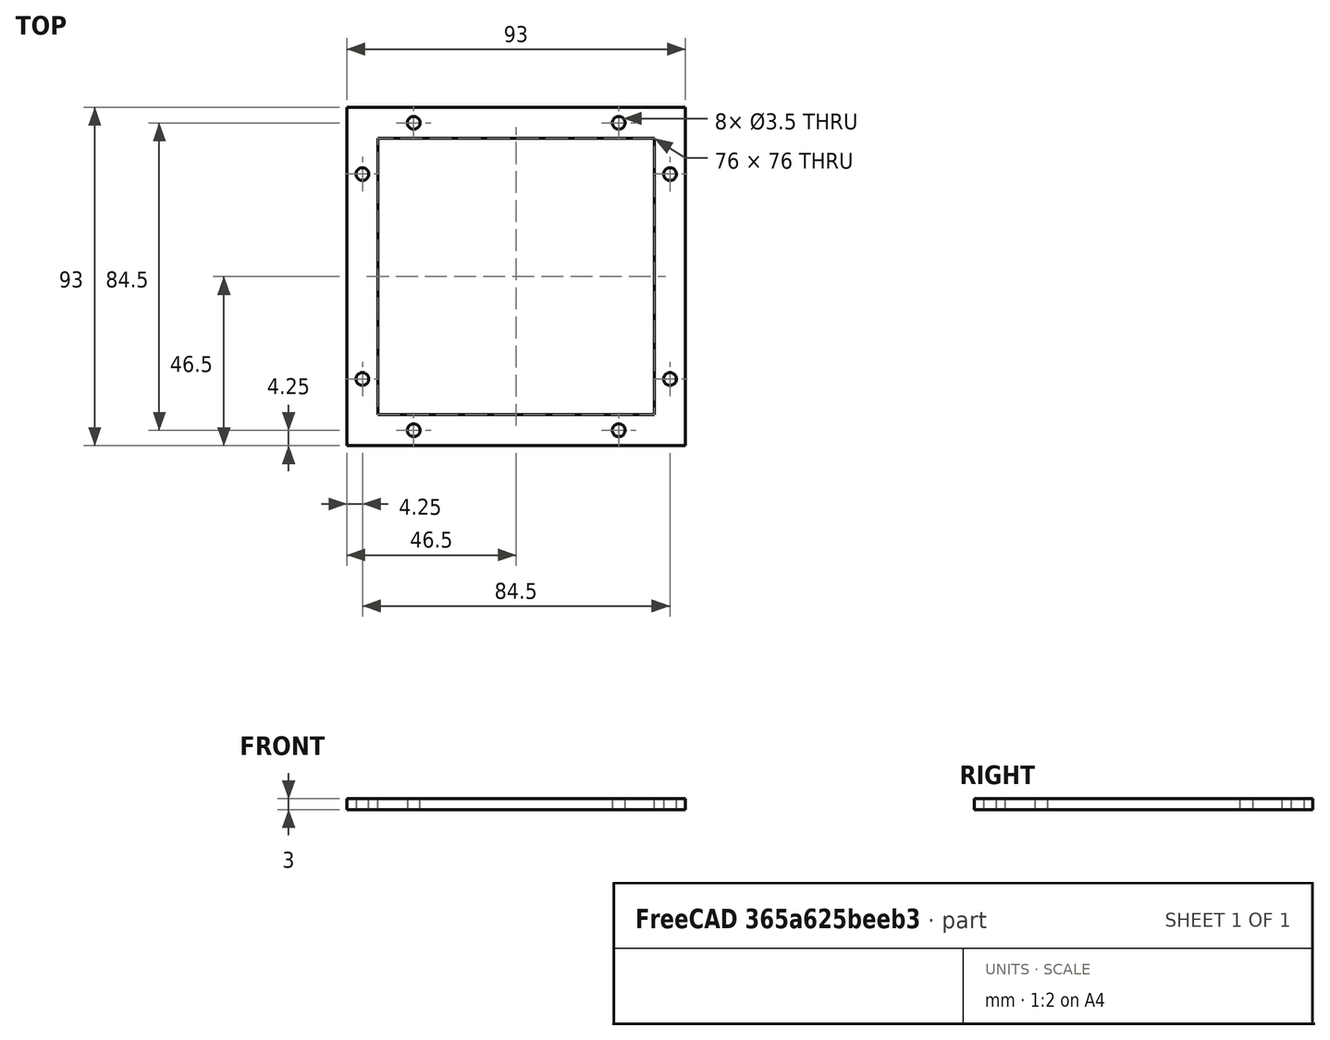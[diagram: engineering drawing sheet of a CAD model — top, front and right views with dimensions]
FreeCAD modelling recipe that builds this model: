
FCSTD DOCUMENT  (FreeCAD 0.14R3141 (Git))
Label: notebook
License: CC-BY 3.0
LicenseURL: http://creativecommons.org/licenses/by/3.0/
objects: Sketcher::SketchObject×3, Drawing::FeatureViewPart×3, PartDesign::Pad×1, Drawing::FeaturePage×1
note: 5 computed .brp shape members not serialized (recipe doc carries the construction recipe); baked Part::Feature solids carry a one-line shape summary decoded from their .brp

FEATURE [Sketcher::SketchObject] Sketch
  sketch-geometry (49):
    g0: LineSegment StartX=-38 StartY=38 StartZ=0 EndX=38 EndY=38 EndZ=0
    g1: LineSegment StartX=38 StartY=38 StartZ=0 EndX=38 EndY=-38 EndZ=0
    g2: LineSegment StartX=38 StartY=-38 StartZ=0 EndX=-38 EndY=-38 EndZ=0
    g3: LineSegment StartX=-38 StartY=-38 StartZ=0 EndX=-38 EndY=38 EndZ=0
    g4: LineSegment [constr] StartX=-38 StartY=0 StartZ=0 EndX=0 EndY=0 EndZ=0
    g5: LineSegment [constr] StartX=0 StartY=0 StartZ=0 EndX=0 EndY=38 EndZ=0
    g6: LineSegment [constr] StartX=0 StartY=0 StartZ=0 EndX=38 EndY=0 EndZ=0
    g7: LineSegment StartX=-46.5 StartY=46.5 StartZ=0 EndX=46.5 EndY=46.5 EndZ=0
    g8: LineSegment StartX=46.5 StartY=46.5 StartZ=0 EndX=46.5 EndY=-46.5 EndZ=0
    g9: LineSegment StartX=46.5 StartY=-46.5 StartZ=0 EndX=-46.5 EndY=-46.5 EndZ=0
    g10: LineSegment StartX=-46.5 StartY=-46.5 StartZ=0 EndX=-46.5 EndY=46.5 EndZ=0
    g11: LineSegment [constr] StartX=-38 StartY=46.5 StartZ=0 EndX=-38 EndY=38 EndZ=0
    g12: LineSegment [constr] StartX=-38 StartY=38 StartZ=0 EndX=-46.5 EndY=38 EndZ=0
    g13: LineSegment [constr] StartX=38 StartY=-38 StartZ=0 EndX=46.5 EndY=-38 EndZ=0
    g14: LineSegment [constr] StartX=-42.25 StartY=46.5 StartZ=0 EndX=-42.25 EndY=42.25 EndZ=0
    g15: LineSegment [constr] StartX=-42.25 StartY=42.25 StartZ=0 EndX=-38 EndY=42.25 EndZ=0
    g16: LineSegment [constr] StartX=-42.25 StartY=42.25 StartZ=0 EndX=-46.5 EndY=42.25 EndZ=0
    g17: LineSegment [constr] StartX=-42.25 StartY=42.25 StartZ=0 EndX=-28.1667 EndY=42.25 EndZ=0
    g18: LineSegment [constr] StartX=-28.1667 StartY=42.25 StartZ=0 EndX=-14.0833 EndY=42.25 EndZ=0
    g19: LineSegment [constr] StartX=-14.0833 StartY=42.25 StartZ=0 EndX=0 EndY=42.25 EndZ=0
    g20: LineSegment [constr] StartX=0 StartY=42.25 StartZ=0 EndX=14.0833 EndY=42.25 EndZ=0
    g21: LineSegment [constr] StartX=14.0833 StartY=42.25 StartZ=0 EndX=28.1667 EndY=42.25 EndZ=0
    g22: LineSegment [constr] StartX=28.1667 StartY=42.25 StartZ=0 EndX=42.25 EndY=42.25 EndZ=0
    g23: LineSegment [constr] StartX=42.25 StartY=42.25 StartZ=0 EndX=42.25 EndY=28.1667 EndZ=0
    g24: LineSegment [constr] StartX=42.25 StartY=28.1667 StartZ=0 EndX=42.25 EndY=14.0833 EndZ=0
    g25: LineSegment [constr] StartX=42.25 StartY=14.0833 StartZ=0 EndX=42.25 EndY=0 EndZ=0
    g26: LineSegment [constr] StartX=42.25 StartY=0 StartZ=0 EndX=42.25 EndY=-14.0833 EndZ=0
    g27: LineSegment [constr] StartX=42.25 StartY=-14.0833 StartZ=0 EndX=42.25 EndY=-28.1667 EndZ=0
    g28: LineSegment [constr] StartX=42.25 StartY=-28.1667 StartZ=0 EndX=42.25 EndY=-42.25 EndZ=0
    g29: LineSegment [constr] StartX=42.25 StartY=-42.25 StartZ=0 EndX=28.1667 EndY=-42.25 EndZ=0
    g30: LineSegment [constr] StartX=28.1667 StartY=-42.25 StartZ=0 EndX=14.0833 EndY=-42.25 EndZ=0
    g31: LineSegment [constr] StartX=14.0833 StartY=-42.25 StartZ=0 EndX=0 EndY=-42.25 EndZ=0
    g32: LineSegment [constr] StartX=0 StartY=-42.25 StartZ=0 EndX=-14.0833 EndY=-42.25 EndZ=0
    g33: LineSegment [constr] StartX=-14.0833 StartY=-42.25 StartZ=0 EndX=-28.1667 EndY=-42.25 EndZ=0
    g34: LineSegment [constr] StartX=-28.1667 StartY=-42.25 StartZ=0 EndX=-42.25 EndY=-42.25 EndZ=0
    g35: LineSegment [constr] StartX=-42.25 StartY=-42.25 StartZ=0 EndX=-42.25 EndY=-28.1667 EndZ=0
    g36: LineSegment [constr] StartX=-42.25 StartY=-28.1667 StartZ=0 EndX=-42.25 EndY=-14.0833 EndZ=0
    g37: LineSegment [constr] StartX=-42.25 StartY=-14.0833 StartZ=0 EndX=-42.25 EndY=0 EndZ=0
    g38: LineSegment [constr] StartX=-42.25 StartY=0 StartZ=0 EndX=-42.25 EndY=14.0833 EndZ=0
    g39: LineSegment [constr] StartX=-42.25 StartY=14.0833 StartZ=0 EndX=-42.25 EndY=28.1667 EndZ=0
    g40: LineSegment [constr] StartX=-42.25 StartY=28.1667 StartZ=0 EndX=-42.25 EndY=42.25 EndZ=0
    g41: Circle CenterX=-28.1667 CenterY=42.25 CenterZ=0 NormalX=0 NormalY=0 NormalZ=1 Radius=1.75
    g42: Circle CenterX=28.1667 CenterY=42.25 CenterZ=0 NormalX=0 NormalY=0 NormalZ=1 Radius=1.75
    g43: Circle CenterX=42.25 CenterY=28.1667 CenterZ=0 NormalX=0 NormalY=0 NormalZ=1 Radius=1.75
    g44: Circle CenterX=42.25 CenterY=-28.1667 CenterZ=0 NormalX=0 NormalY=0 NormalZ=1 Radius=1.75
    g45: Circle CenterX=28.1667 CenterY=-42.25 CenterZ=0 NormalX=0 NormalY=0 NormalZ=1 Radius=1.75
    g46: Circle CenterX=-28.1667 CenterY=-42.25 CenterZ=0 NormalX=0 NormalY=0 NormalZ=1 Radius=1.75
    g47: Circle CenterX=-42.25 CenterY=-28.1667 CenterZ=0 NormalX=0 NormalY=0 NormalZ=1 Radius=1.75
    g48: Circle CenterX=-42.25 CenterY=28.1667 CenterZ=0 NormalX=0 NormalY=0 NormalZ=1 Radius=1.75
  constraints (139):
    c: Coincident(g0,g1)
    c: Coincident(g1,g2)
    c: Coincident(g2,g3)
    c: Coincident(g3,g0)
    c: Horizontal(g0)
    c: Horizontal(g2)
    c: Vertical(g1)
    c: Vertical(g3)
    c: PointOnObject(g4,g3)
    c: Coincident(g4,g-1)
    c: Horizontal(g4)
    c: Coincident(g4,g5)
    c: PointOnObject(g5,g0)
    c: Vertical(g5)
    c: Coincident(g6,g-1)
    c: PointOnObject(g6,g1)
    c: Horizontal(g6)
    c: Equal(g5,g4)
    c: Equal(g6,g5)
    c: Equal(g2,g3)
    c: DistanceY(g3) = 76
    c: Coincident(g7,g8)
    c: Coincident(g8,g9)
    c: Coincident(g9,g10)
    c: Coincident(g10,g7)
    c: Horizontal(g7)
    c: Horizontal(g9)
    c: Vertical(g8)
    c: Vertical(g10)
    c: Equal(g9,g10)
    c: PointOnObject(g11,g7)
    c: Coincident(g11,g0)
    c: Vertical(g11)
    c: Coincident(g11,g12)
    c: PointOnObject(g12,g10)
    c: Horizontal(g12)
    c: Equal(g11,g12)
    c: Coincident(g13,g1)
    c: PointOnObject(g13,g8)
    c: Horizontal(g13)
    c: Equal(g13,g11)
    c: DistanceY(g11) = -8.5
    c: PointOnObject(g14,g7)
    c: Vertical(g14)
    c: Coincident(g15,g14)
    c: PointOnObject(g15,g11)
    c: Horizontal(g15)
    c: Coincident(g16,g14)
    c: PointOnObject(g16,g10)
    c: Horizontal(g16)
    c: Equal(g16,g14)
    c: Equal(g14,g15)
    c: Coincident(g14,g17)
    c: Horizontal(g17)
    c: Coincident(g17,g18)
    c: Horizontal(g18)
    c: Coincident(g18,g19)
    c: Horizontal(g19)
    c: Coincident(g19,g20)
    c: Horizontal(g20)
    c: Coincident(g20,g21)
    c: Horizontal(g21)
    c: Coincident(g21,g22)
    c: Horizontal(g22)
    c: Coincident(g22,g23)
    c: Vertical(g23)
    c: Coincident(g23,g24)
    c: Vertical(g24)
    c: Coincident(g24,g25)
    c: Vertical(g25)
    c: Coincident(g25,g26)
    c: Vertical(g26)
    c: Coincident(g26,g27)
    c: Vertical(g27)
    c: Coincident(g27,g28)
    c: Vertical(g28)
    c: Coincident(g28,g29)
    c: Horizontal(g29)
    c: Coincident(g29,g30)
    c: Horizontal(g30)
    c: Coincident(g30,g31)
    c: PointOnObject(g31,g-2)
    c: Horizontal(g31)
    c: Coincident(g31,g32)
    c: Horizontal(g32)
    c: Coincident(g32,g33)
    c: Horizontal(g33)
    c: Coincident(g33,g34)
    c: Horizontal(g34)
    c: Coincident(g34,g35)
    c: Vertical(g35)
    c: Coincident(g35,g36)
    c: Vertical(g36)
    c: Coincident(g36,g37)
    c: PointOnObject(g37,g-1)
    c: Vertical(g37)
    c: Coincident(g37,g38)
    c: Vertical(g38)
    c: Coincident(g38,g39)
    c: Vertical(g39)
    c: Coincident(g39,g40)
    c: Coincident(g40,g14)
    c: Vertical(g40)
    c: PointOnObject(g19,g-2)
    c: PointOnObject(g25,g-1)
    c: Equal(g17,g18)
    c: Equal(g18,g19)
    c: Equal(g20,g21)
    c: Equal(g21,g22)
    c: Equal(g20,g19)
    c: Equal(g23,g24)
    c: Equal(g24,g25)
    c: Equal(g25,g26)
    c: Equal(g26,g27)
    c: Equal(g27,g28)
    c: Equal(g29,g30)
    c: Equal(g30,g31)
    c: Equal(g32,g33)
    c: Equal(g35,g36)
    c: Equal(g36,g37)
    c: Equal(g40,g39)
    c: Equal(g39,g38)
    c: Equal(g34,g33)
    c: Coincident(g41,g17)
    c: Coincident(g42,g21)
    c: Coincident(g43,g23)
    c: Coincident(g44,g27)
    c: Coincident(g45,g29)
    c: Coincident(g46,g33)
    c: Coincident(g47,g35)
    c: Coincident(g48,g39)
    c: Radius(g41) = 1.75
    c: Equal(g42,g43)
    c: Equal(g44,g45)
    c: Equal(g46,g47)
    c: Equal(g41,g42)
    c: Equal(g43,g44)
    c: Equal(g45,g46)
    c: Equal(g47,g48)
FEATURE [PartDesign::Pad] Pad  label="Base data"
  Length = 3
  Length2 = 100
  Sketch = -> Sketch
  Type = 0
FEATURE [Sketcher::SketchObject] Sketch001  label="Everything"
  ExternalGeometry = -> [Pad]
  Placement = pos=(0,0,3) rot=(0,0,1;0rad)
  Support = -> Pad [Face18]
  sketch-geometry (62):
    g0: LineSegment StartX=-49.5 StartY=49.5 StartZ=0 EndX=49.5 EndY=49.5 EndZ=0
    g1: LineSegment [constr] StartX=49.5 StartY=49.5 StartZ=0 EndX=49.5 EndY=-49.5 EndZ=0
    g2: LineSegment StartX=49.5 StartY=-49.5 StartZ=0 EndX=-49.5 EndY=-49.5 EndZ=0
    g3: LineSegment [constr] StartX=-49.5 StartY=-49.5 StartZ=0 EndX=-49.5 EndY=49.5 EndZ=0
    g4: LineSegment [constr] StartX=-46.5 StartY=49.5 StartZ=0 EndX=-46.5 EndY=46.5 EndZ=0
    g5: LineSegment [constr] StartX=-46.5 StartY=46.5 StartZ=0 EndX=-49.5 EndY=46.5 EndZ=0
    g6: LineSegment [constr] StartX=46.5 StartY=-46.5 StartZ=0 EndX=49.5 EndY=-46.5 EndZ=0
    g7: LineSegment StartX=49.5 StartY=49.5 StartZ=0 EndX=69.5 EndY=49.5 EndZ=0
    g8: LineSegment [constr] StartX=69.5 StartY=49.5 StartZ=0 EndX=69.5 EndY=-49.5 EndZ=0
    g9: LineSegment StartX=69.5 StartY=-49.5 StartZ=0 EndX=49.5 EndY=-49.5 EndZ=0
    g10: LineSegment StartX=69.5 StartY=49.5 StartZ=0 EndX=165.5 EndY=49.5 EndZ=0
    g11: LineSegment StartX=168.5 StartY=46.5 StartZ=0 EndX=168.5 EndY=-46.5 EndZ=0
    g12: LineSegment StartX=165.5 StartY=-49.5 StartZ=0 EndX=69.5 EndY=-49.5 EndZ=0
    g13: ArcOfCircle CenterX=165.5 CenterY=46.5 CenterZ=0 NormalX=0 NormalY=0 NormalZ=1 Radius=3 StartAngle=0 EndAngle=1.5708
    g14: ArcOfCircle CenterX=165.5 CenterY=-46.5 CenterZ=0 NormalX=0 NormalY=0 NormalZ=1 Radius=3 StartAngle=4.71239 EndAngle=6.28319
    g15: LineSegment StartX=72.5 StartY=-46.5 StartZ=0 EndX=165.5 EndY=-46.5 EndZ=0
    g16: LineSegment StartX=165.5 StartY=-46.5 StartZ=0 EndX=165.5 EndY=46.5 EndZ=0
    g17: LineSegment StartX=165.5 StartY=46.5 StartZ=0 EndX=150.5 EndY=46.5 EndZ=0
    g18: LineSegment StartX=72.5 StartY=-31.5 StartZ=0 EndX=72.5 EndY=-46.5 EndZ=0
    g19: LineSegment [constr] StartX=72.5 StartY=-46.5 StartZ=0 EndX=69.5 EndY=-46.5 EndZ=0
    g20: LineSegment [constr] StartX=161.25 StartY=42.25 StartZ=0 EndX=161.25 EndY=14.0833 EndZ=0
    g21: LineSegment [constr] StartX=161.25 StartY=14.0833 StartZ=0 EndX=161.25 EndY=-14.0833 EndZ=0
    g22: LineSegment [constr] StartX=161.25 StartY=-14.0833 StartZ=0 EndX=161.25 EndY=-42.25 EndZ=0
    g23: LineSegment [constr] StartX=161.25 StartY=-42.25 StartZ=0 EndX=133.083 EndY=-42.25 EndZ=0
    g24: LineSegment [constr] StartX=133.083 StartY=-42.25 StartZ=0 EndX=104.917 EndY=-42.25 EndZ=0
    g25: LineSegment [constr] StartX=104.917 StartY=-42.25 StartZ=0 EndX=76.75 EndY=-42.25 EndZ=0
    g26: LineSegment [constr] StartX=-28.1667 StartY=42.25 StartZ=0 EndX=0 EndY=42.25 EndZ=0
    g27: LineSegment [constr] StartX=161.25 StartY=-46.5 StartZ=0 EndX=161.25 EndY=-42.25 EndZ=0
    g28: LineSegment [constr] StartX=161.25 StartY=-42.25 StartZ=0 EndX=165.5 EndY=-42.25 EndZ=0
    g29: Circle CenterX=161.25 CenterY=42.25 CenterZ=0 NormalX=0 NormalY=0 NormalZ=1 Radius=1.75
    g30: Circle CenterX=161.25 CenterY=14.0833 CenterZ=0 NormalX=0 NormalY=0 NormalZ=1 Radius=1.75
    g31: Circle CenterX=161.25 CenterY=-14.0833 CenterZ=0 NormalX=0 NormalY=0 NormalZ=1 Radius=1.75
    g32: Circle CenterX=161.25 CenterY=-42.25 CenterZ=0 NormalX=0 NormalY=0 NormalZ=1 Radius=1.75
    g33: Circle CenterX=133.083 CenterY=-42.25 CenterZ=0 NormalX=0 NormalY=0 NormalZ=1 Radius=1.75
    g34: Circle CenterX=104.917 CenterY=-42.25 CenterZ=0 NormalX=0 NormalY=0 NormalZ=1 Radius=1.75
    g35: Circle CenterX=76.75 CenterY=-42.25 CenterZ=0 NormalX=0 NormalY=0 NormalZ=1 Radius=1.75
    g36: LineSegment StartX=66 StartY=34.5 StartZ=0 EndX=53 EndY=34.5 EndZ=0
    g37: LineSegment [constr] StartX=53 StartY=34.5 StartZ=0 EndX=53 EndY=24.5 EndZ=0
    g38: LineSegment StartX=53 StartY=24.5 StartZ=0 EndX=66 EndY=24.5 EndZ=0
    g39: LineSegment [constr] StartX=66 StartY=34.5 StartZ=0 EndX=69.5 EndY=34.5 EndZ=0
    g40: LineSegment [constr] StartX=53 StartY=34.5 StartZ=0 EndX=49.5 EndY=34.5 EndZ=0
    g41: ArcOfCircle CenterX=53 CenterY=36 CenterZ=0 NormalX=0 NormalY=0 NormalZ=1 Radius=1.5 StartAngle=3.66519 EndAngle=4.71239
    g42: ArcOfCircle CenterX=50.4019 CenterY=34.5 CenterZ=0 NormalX=0 NormalY=0 NormalZ=1 Radius=1.5 StartAngle=0.523596 EndAngle=5.75958
    g43: ArcOfCircle CenterX=53 CenterY=33 CenterZ=0 NormalX=0 NormalY=0 NormalZ=1 Radius=1.5 StartAngle=1.5708 EndAngle=2.618
    g44: ArcOfCircle CenterX=68.5981 CenterY=34.5 CenterZ=0 NormalX=0 NormalY=0 NormalZ=1 Radius=1.5 StartAngle=3.66519 EndAngle=8.90118
    g45: ArcOfCircle CenterX=66 CenterY=36 CenterZ=0 NormalX=0 NormalY=0 NormalZ=1 Radius=1.5 StartAngle=4.71239 EndAngle=5.75958
    g46: ArcOfCircle CenterX=66 CenterY=33 CenterZ=0 NormalX=0 NormalY=0 NormalZ=1 Radius=1.5 StartAngle=0.523597 EndAngle=1.5708
    g47: ArcOfCircle CenterX=68.5981 CenterY=24.5 CenterZ=0 NormalX=0 NormalY=0 NormalZ=1 Radius=1.5 StartAngle=3.66519 EndAngle=8.90118
    g48: ArcOfCircle CenterX=66 CenterY=26 CenterZ=0 NormalX=0 NormalY=0 NormalZ=1 Radius=1.5 StartAngle=4.71239 EndAngle=5.75959
    g49: ArcOfCircle CenterX=66 CenterY=23 CenterZ=0 NormalX=0 NormalY=0 NormalZ=1 Radius=1.5 StartAngle=0.523598 EndAngle=1.5708
    g50: ArcOfCircle CenterX=50.4019 CenterY=24.5 CenterZ=0 NormalX=0 NormalY=0 NormalZ=1 Radius=1.5 StartAngle=0.523599 EndAngle=5.75959
    g51: ArcOfCircle CenterX=53 CenterY=26 CenterZ=0 NormalX=0 NormalY=0 NormalZ=1 Radius=1.5 StartAngle=3.66519 EndAngle=4.71239
    g52: ArcOfCircle CenterX=53 CenterY=23 CenterZ=0 NormalX=0 NormalY=0 NormalZ=1 Radius=1.5 StartAngle=1.5708 EndAngle=2.61799
    g53: ArcOfCircle CenterX=-49.5 CenterY=39.5 CenterZ=0 NormalX=0 NormalY=0 NormalZ=1 Radius=10 StartAngle=1.5708 EndAngle=2.5806
    g54: ArcOfCircle CenterX=-49.5 CenterY=-39.5 CenterZ=0 NormalX=0 NormalY=0 NormalZ=1 Radius=10 StartAngle=3.70258 EndAngle=4.71239
    g55: LineSegment StartX=-57.9673 StartY=44.8202 StartZ=0 EndX=-83.1206 EndY=4.78822 EndZ=0
    g56: LineSegment StartX=-83.1206 StartY=-4.78822 StartZ=0 EndX=-57.9673 EndY=-44.8202 EndZ=0
    g57: ArcOfCircle CenterX=-75.5 CenterY=0 CenterZ=0 NormalX=0 NormalY=0 NormalZ=1 Radius=9 StartAngle=2.5806 EndAngle=3.70258
    g58: Circle CenterX=-75.5 CenterY=0 CenterZ=0 NormalX=0 NormalY=0 NormalZ=1 Radius=1.75
    g59: LineSegment [constr] StartX=-70.5 StartY=24.8741 StartZ=0 EndX=-70.5 EndY=-24.8741 EndZ=0
    g60: Circle CenterX=158.5 CenterY=0 CenterZ=0 NormalX=0 NormalY=0 NormalZ=1 Radius=1.75
    g61: ArcOfCircle CenterX=217.703 CenterY=-98.7026 CenterZ=0 NormalX=0 NormalY=0 NormalZ=1 Radius=160 StartAngle=2.00426 EndAngle=2.70813
  constraints (184):
    c: Coincident(g0,g1)
    c: Coincident(g1,g2)
    c: Coincident(g2,g3)
    c: Coincident(g3,g0)
    c: Horizontal(g0)
    c: Horizontal(g2)
    c: Vertical(g1)
    c: Vertical(g3)
    c: PointOnObject(g4,g0)
    c: Coincident(g4,g-6)
    c: Vertical(g4)
    c: Coincident(g4,g5)
    c: Horizontal(g5)
    c: Equal(g5,g4)
    c: PointOnObject(g5,g3)
    c: Equal(g3,g2)
    c: Coincident(g6,g-5)
    c: PointOnObject(g6,g1)
    c: Horizontal(g6)
    c: Equal(g6,g4)
    c: Coincident(g0,g7)
    c: Horizontal(g7)
    c: Coincident(g7,g8)
    c: Vertical(g8)
    c: Coincident(g8,g9)
    c: Coincident(g9,g1)
    c: Horizontal(g9)
    c: DistanceX(g7) = 20
    c: Coincident(g7,g10)
    c: Horizontal(g10)
    c: Vertical(g11)
    c: Coincident(g12,g8)
    c: Horizontal(g12)
    c: Tangent(g10,g13)
    c: Tangent(g11,g13)
    c: Tangent(g11,g14)
    c: Tangent(g12,g14)
    c: Horizontal(g15)
    c: Coincident(g15,g16)
    c: Vertical(g16)
    c: Coincident(g16,g17)
    c: Horizontal(g17)
    c: Vertical(g18)
    c: Coincident(g15,g18)
    c: PointOnObject(g15,g-5)
    c: PointOnObject(g16,g-3)
    c: Equal(g15,g16)
    c: Equal(g18,g17)
    c: Coincident(g13,g16)
    c: Equal(g14,g13)
    c: Coincident(g19,g15)
    c: PointOnObject(g19,g8)
    c: Horizontal(g19)
    c: Equal(g19,g6)
    c: DistanceX(g17) = -15
    c: Coincident(g20,g21)
    c: Coincident(g21,g22)
    c: Coincident(g22,g23)
    c: Coincident(g23,g24)
    c: Coincident(g24,g25)
    c: Vertical(g22)
    c: Vertical(g21)
    c: Vertical(g20)
    c: Horizontal(g23)
    c: Horizontal(g24)
    c: Horizontal(g25)
    c: Coincident(g26,g-7)
    c: PointOnObject(g20,g26)
    c: Equal(g20,g26)
    c: Equal(g20,g21)
    c: Equal(g21,g22)
    c: Equal(g23,g22)
    c: Equal(g23,g24)
    c: Equal(g24,g25)
    c: Coincident(g27,g28)
    c: PointOnObject(g27,g15)
    c: Coincident(g27,g22)
    c: PointOnObject(g28,g16)
    c: Horizontal(g28)
    c: Vertical(g27)
    c: Equal(g27,g28)
    c: DistanceX(g5) = -3
    c: Coincident(g29,g20)
    c: Coincident(g30,g20)
    c: Coincident(g31,g21)
    c: Coincident(g32,g22)
    c: Coincident(g33,g23)
    c: Coincident(g34,g24)
    c: Coincident(g35,g25)
    c: Equal(g29,g30)
    c: Equal(g30,g31)
    c: Equal(g31,g32)
    c: Equal(g33,g32)
    c: Equal(g33,g34)
    c: Equal(g34,g35)
    c: Horizontal(g36)
    c: Coincident(g36,g37)
    c: Vertical(g37)
    c: Coincident(g37,g38)
    c: Horizontal(g38)
    c: Equal(g38,g36)
    c: Coincident(g39,g36)
    c: PointOnObject(g39,g8)
    c: Horizontal(g39)
    c: Coincident(g40,g36)
    c: PointOnObject(g40,g1)
    c: Horizontal(g40)
    c: Equal(g40,g39)
    c: Coincident(g41,g36)
    c: PointOnObject(g42,g40)
    c: Coincident(g42,g41)
    c: Coincident(g43,g36)
    c: Coincident(g43,g42)
    c: Tangent(g43,g42)
    c: Tangent(g41,g42)
    c: Tangent(g41,g36)
    c: Tangent(g43,g36)
    c: DistanceY(g37) = -10
    c: DistanceY(g39,g7) = 15
    c: Equal(g41,g42)
    c: Radius(g42) = 1.5
    c: PointOnObject(g44,g39)
    c: Coincident(g45,g36)
    c: Coincident(g46,g36)
    c: Coincident(g44,g45)
    c: Coincident(g46,g44)
    c: Equal(g45,g44)
    c: Equal(g46,g45)
    c: Tangent(g45,g44)
    c: Tangent(g46,g44)
    c: Tangent(g45,g36)
    c: Equal(g44,g42)
    c: DistanceX(g36) = -13
    c: Coincident(g48,g38)
    c: Coincident(g49,g38)
    c: Coincident(g48,g47)
    c: Coincident(g49,g47)
    c: Equal(g48,g49)
    c: Equal(g48,g47)
    c: Equal(g47,g44)
    c: Tangent(g48,g47)
    c: Tangent(g49,g47)
    c: Tangent(g49,g38)
    c: Tangent(g48,g38)
    c: Coincident(g51,g37)
    c: Coincident(g52,g37)
    c: Coincident(g51,g50)
    c: Coincident(g52,g50)
    c: Equal(g50,g51)
    c: Equal(g51,g52)
    c: Equal(g50,g42)
    c: Tangent(g51,g50)
    c: Tangent(g52,g50)
    c: Tangent(g51,g38)
    c: Tangent(g52,g38)
    c: PointOnObject(g53,g3)
    c: Coincident(g53,g0)
    c: PointOnObject(g54,g3)
    c: Coincident(g54,g2)
    c: Equal(g54,g53)
    c: Tangent(g53,g55)
    c: Coincident(g56,g54)
    c: Tangent(g56,g54)
    c: Tangent(g55,g57)
    c: Tangent(g56,g57)
    c: PointOnObject(g57,g-1)
    c: Coincident(g58,g57)
    c: Radius(g53) = 10
    c: Vertical(g59)
    c: PointOnObject(g59,g55)
    c: PointOnObject(g59,g56)
    c: DistanceX(g57,g59) = 5
    c: Radius(g58) = 1.75
    c: Radius(g57) = 9
    c: PointOnObject(g60,g-1)
    c: Equal(g58,g60)
    c: Coincident(g61,g17)
    c: Coincident(g61,g18)
    c: Radius(g61) = 160
    c: DistanceX(g59,g2) = 21
    c: DistanceX(g60,g14) = 7
    c: Horizontal(g26)
    c: PointOnObject(g26,g-2)
    c: Equal(g-7,g35)
FEATURE [Drawing::FeatureViewPart] View  label="View: Base"
  Direction = (0,0,-1)
  HiddenWidth = 0.15
  LineWidth = 0.35
  Rotation = 270
  ShowHiddenLines = false
  ShowSmoothLines = false
  Source = -> Pad
  Tolerance = 0.05
  ViewResult = <g id="View: Base"    transform="rotate(270,50,251) translate(50,251) scale(1,1)"   > <g   stroke="rgb(0, 0, 0)"    stroke-width="0.35"    stroke-linecap="butt"    stroke-linejoin="miter"    fill="none"    transform="scale(1,-1)"   > <path id= "1" d=" M 46.5 46.5 L -46.5 46.5 " /> <path id= "2" d=" M -46.5 46.5 L -46.5 -46.5 " /> <path id= "3" d=" M -46.5 -46.5 L 46.5 -46.5 " /> <path id= "4" d=" M 46.5 -46.5 L 46.5 46.5 " /> <path id= "5" d=" M 38 38 L -38 38 " /> <path id= "6" d=" M -38 38 L -38 -38 " /> <path id= "7" d=" M -38 -38 L 38 -38 " /> <path id= "8" d=" M 38 -38 L 38 38 " /> <circle cx ="42.25" cy ="28.1667" r ="1.75" /><circle cx ="42.25" cy ="-28.1667" r ="1.75" /><circle cx ="28.1667" cy ="-42.25" r ="1.75" /><circle cx ="-28.1667" cy ="-42.25" r ="1.75" /><circle cx ="-42.25" cy ="-28.1667" r ="1.75" /><circle cx ="-42.25" cy ="28.1667" r ="1.75" /><circle cx ="-28.1667" cy ="42.25" r ="1.75" /><circle cx ="28.1667" cy ="42.25" r ="1.75" /></g> </g> 
  X = 50
  Y = 251
FEATURE [Drawing::FeatureViewPart] View001  label="View: Everything"
  Direction = (0,0,-1)
  HiddenWidth = 0.15
  LineWidth = 0.35
  Rotation = 270
  ShowHiddenLines = false
  ShowSmoothLines = false
  Source = -> Sketch001
  Tolerance = 0.05
  ViewResult = <blob: 2383 chars omitted>
  X = 50
  Y = 251
FEATURE [Sketcher::SketchObject] Sketch002  label="Border"
  ExternalGeometry = -> [Pad]
  Placement = pos=(0,0,3) rot=(0,0,1;0rad)
  Support = -> Pad [Face18]
  sketch-geometry (24):
    g0: ArcOfCircle CenterX=-23.5 CenterY=38 CenterZ=0 NormalX=0 NormalY=0 NormalZ=1 Radius=8.5 StartAngle=0 EndAngle=1.5708
    g1: LineSegment StartX=-15 StartY=38 StartZ=0 EndX=-38 EndY=38 EndZ=0
    g2: LineSegment StartX=-38 StartY=38 StartZ=0 EndX=-38 EndY=15 EndZ=0
    g3: LineSegment StartX=-23.5 StartY=46.5 StartZ=0 EndX=-46.5 EndY=46.5 EndZ=0
    g4: LineSegment StartX=-46.5 StartY=46.5 StartZ=0 EndX=-46.5 EndY=23.5 EndZ=0
    g5: ArcOfCircle CenterX=-38 CenterY=23.5 CenterZ=0 NormalX=0 NormalY=0 NormalZ=1 Radius=8.5 StartAngle=3.1416 EndAngle=4.71239
    g6: LineSegment StartX=15 StartY=38 StartZ=0 EndX=38 EndY=38 EndZ=0
    g7: LineSegment StartX=38 StartY=38 StartZ=0 EndX=38 EndY=15 EndZ=0
    g8: ArcOfCircle CenterX=23.5 CenterY=38 CenterZ=0 NormalX=0 NormalY=0 NormalZ=1 Radius=8.5 StartAngle=1.5708 EndAngle=3.14159
    g9: ArcOfCircle CenterX=38 CenterY=23.5 CenterZ=0 NormalX=0 NormalY=0 NormalZ=1 Radius=8.5 StartAngle=4.71239 EndAngle=6.28318
    g10: LineSegment StartX=23.5 StartY=46.5 StartZ=0 EndX=46.5 EndY=46.5 EndZ=0
    g11: LineSegment StartX=46.5 StartY=46.5 StartZ=0 EndX=46.5 EndY=23.5 EndZ=0
    g12: LineSegment StartX=-38 StartY=-15 StartZ=0 EndX=-38 EndY=-38 EndZ=0
    g13: LineSegment StartX=-38 StartY=-38 StartZ=0 EndX=-15 EndY=-38 EndZ=0
    g14: LineSegment StartX=-46.5 StartY=-23.5 StartZ=0 EndX=-46.5 EndY=-46.5 EndZ=0
    g15: LineSegment StartX=-46.5 StartY=-46.5 StartZ=0 EndX=-23.5 EndY=-46.5 EndZ=0
    g16: ArcOfCircle CenterX=-38 CenterY=-23.5 CenterZ=0 NormalX=0 NormalY=0 NormalZ=1 Radius=8.5 StartAngle=1.5708 EndAngle=3.14159
    g17: ArcOfCircle CenterX=-23.5 CenterY=-38 CenterZ=0 NormalX=0 NormalY=0 NormalZ=1 Radius=8.5 StartAngle=4.71239 EndAngle=6.28319
    g18: LineSegment StartX=38 StartY=-15 StartZ=0 EndX=38 EndY=-38 EndZ=0
    g19: LineSegment StartX=38 StartY=-38 StartZ=0 EndX=15 EndY=-38 EndZ=0
    g20: LineSegment StartX=23.5 StartY=-46.5 StartZ=0 EndX=46.5 EndY=-46.5 EndZ=0
    g21: LineSegment StartX=46.5 StartY=-46.5 StartZ=0 EndX=46.5 EndY=-23.5 EndZ=0
    g22: ArcOfCircle CenterX=38 CenterY=-23.5 CenterZ=0 NormalX=0 NormalY=0 NormalZ=1 Radius=8.5 StartAngle=4.82221e-06 EndAngle=1.5708
    g23: ArcOfCircle CenterX=23.5 CenterY=-38 CenterZ=0 NormalX=0 NormalY=0 NormalZ=1 Radius=8.5 StartAngle=3.14159 EndAngle=4.71238
  constraints (70):
    c: Horizontal(g1)
    c: Coincident(g1,g2)
    c: Vertical(g2)
    c: PointOnObject(g0,g1)
    c: Coincident(g0,g1)
    c: Tangent(g0,g3)
    c: Coincident(g3,g4)
    c: Vertical(g4)
    c: Horizontal(g3)
    c: PointOnObject(g5,g2)
    c: Coincident(g5,g2)
    c: Coincident(g5,g4)
    c: Equal(g1,g2)
    c: Coincident(g1,g-4)
    c: Coincident(g3,g-6)
    c: Tangent(g4,g5)
    c: Horizontal(g6)
    c: Coincident(g6,g7)
    c: Vertical(g7)
    c: PointOnObject(g8,g6)
    c: Coincident(g8,g6)
    c: PointOnObject(g9,g7)
    c: Coincident(g9,g7)
    c: Tangent(g8,g10)
    c: Coincident(g10,g11)
    c: Coincident(g11,g9)
    c: Equal(g7,g6)
    c: Vertical(g11)
    c: Horizontal(g10)
    c: Tangent(g9,g11)
    c: Equal(g6,g1)
    c: Coincident(g6,g-8)
    c: Coincident(g10,g-7)
    c: Vertical(g12)
    c: Coincident(g12,g13)
    c: Horizontal(g13)
    c: Vertical(g14)
    c: Coincident(g14,g15)
    c: Horizontal(g15)
    c: PointOnObject(g16,g12)
    c: Coincident(g16,g12)
    c: Coincident(g16,g14)
    c: PointOnObject(g17,g13)
    c: Coincident(g17,g13)
    c: Coincident(g17,g15)
    c: Tangent(g17,g15)
    c: Tangent(g14,g16)
    c: Equal(g12,g13)
    c: Equal(g12,g2)
    c: Coincident(g12,g-9)
    c: Coincident(g14,g-10)
    c: Vertical(g18)
    c: Coincident(g18,g19)
    c: Horizontal(g19)
    c: Horizontal(g20)
    c: Coincident(g20,g21)
    c: Vertical(g21)
    c: PointOnObject(g22,g18)
    c: Coincident(g22,g18)
    c: Coincident(g22,g21)
    c: PointOnObject(g23,g19)
    c: Coincident(g23,g19)
    c: Coincident(g23,g20)
    c: Tangent(g23,g20)
    c: Tangent(g22,g21)
    c: Coincident(g18,g-9)
    c: Coincident(g20,g-10)
    c: Equal(g18,g19)
    c: Equal(g18,g7)
    c: DistanceX(g0,g6) = 30
FEATURE [Drawing::FeatureViewPart] Ortho  label="View: Border"
  Direction = (0,0,-1)
  HiddenWidth = 0.15
  LineWidth = 0.35
  Rotation = 270
  ShowHiddenLines = false
  ShowSmoothLines = false
  Source = -> Sketch002
  Tolerance = 0.05
  ViewResult = <g id="View: Border"    transform="rotate(270,50,251) translate(50,251) scale(1,1)"   > <g   stroke="rgb(0, 0, 0)"    stroke-width="0.35"    stroke-linecap="butt"    stroke-linejoin="miter"    fill="none"    transform="scale(1,-1)"   > <path d="M15 38 A8.5 8.5 0 0 0 23.5 46.5" /><path id= "2" d=" M 23.5 46.5 L 46.5 46.5 " /> <path id= "3" d=" M 46.5 46.5 L 46.5 23.5 " /> <path d="M46.5 23.5 A8.5 8.5 0 0 0 38 15" /><path id= "5" d=" M 38 38 L 38 15 " /> <path id= "6" d=" M 15 38 L 38 38 " /> <path id= "7" d=" M -15 38 L -38 38 " /> <path id= "8" d=" M -38 38 L -38 15 " /> <path d="M-38 15 A8.5 8.5 0 0 0 -46.5 23.5" /><path id= "10" d=" M -46.5 46.5 L -46.5 23.5 " /> <path id= "11" d=" M -23.5 46.5 L -46.5 46.5 " /> <path d="M-23.5 46.5 A8.5 8.5 0 0 0 -15 38" /><path d="M38 -15 A8.5 8.5 0 0 0 46.5 -23.5" /><path id= "14" d=" M 38 -15 L 38 -38 " /> <path id= "15" d=" M 38 -38 L 15 -38 " /> <path d="M23.5 -46.5 A8.5 8.5 0 0 0 15 -38" /><path id= "17" d=" M 46.5 -46.5 L 23.5 -46.5 " /> <path id= "18" d=" M 46.5 -23.5 L 46.5 -46.5 " /> <path id= "19" d=" M -38 -15 L -38 -38 " /> <path id= "20" d=" M -38 -38 L -15 -38 " /> <path d="M-15 -38 A8.5 8.5 0 0 0 -23.5 -46.5" /><path id= "22" d=" M -23.5 -46.5 L -46.5 -46.5 " /> <path id= "23" d=" M -46.5 -46.5 L -46.5 -23.5 " /> <path d="M-46.5 -23.5 A8.5 8.5 0 0 0 -38 -15" /></g> </g> 
  X = 50
  Y = 251
FEATURE [Drawing::FeaturePage] Page
  Group = -> [View,View001,Ortho]
  Template = <path>
note: 1 file-system path scrubbed to <path> (originals preserved in the JSON sidecar)
